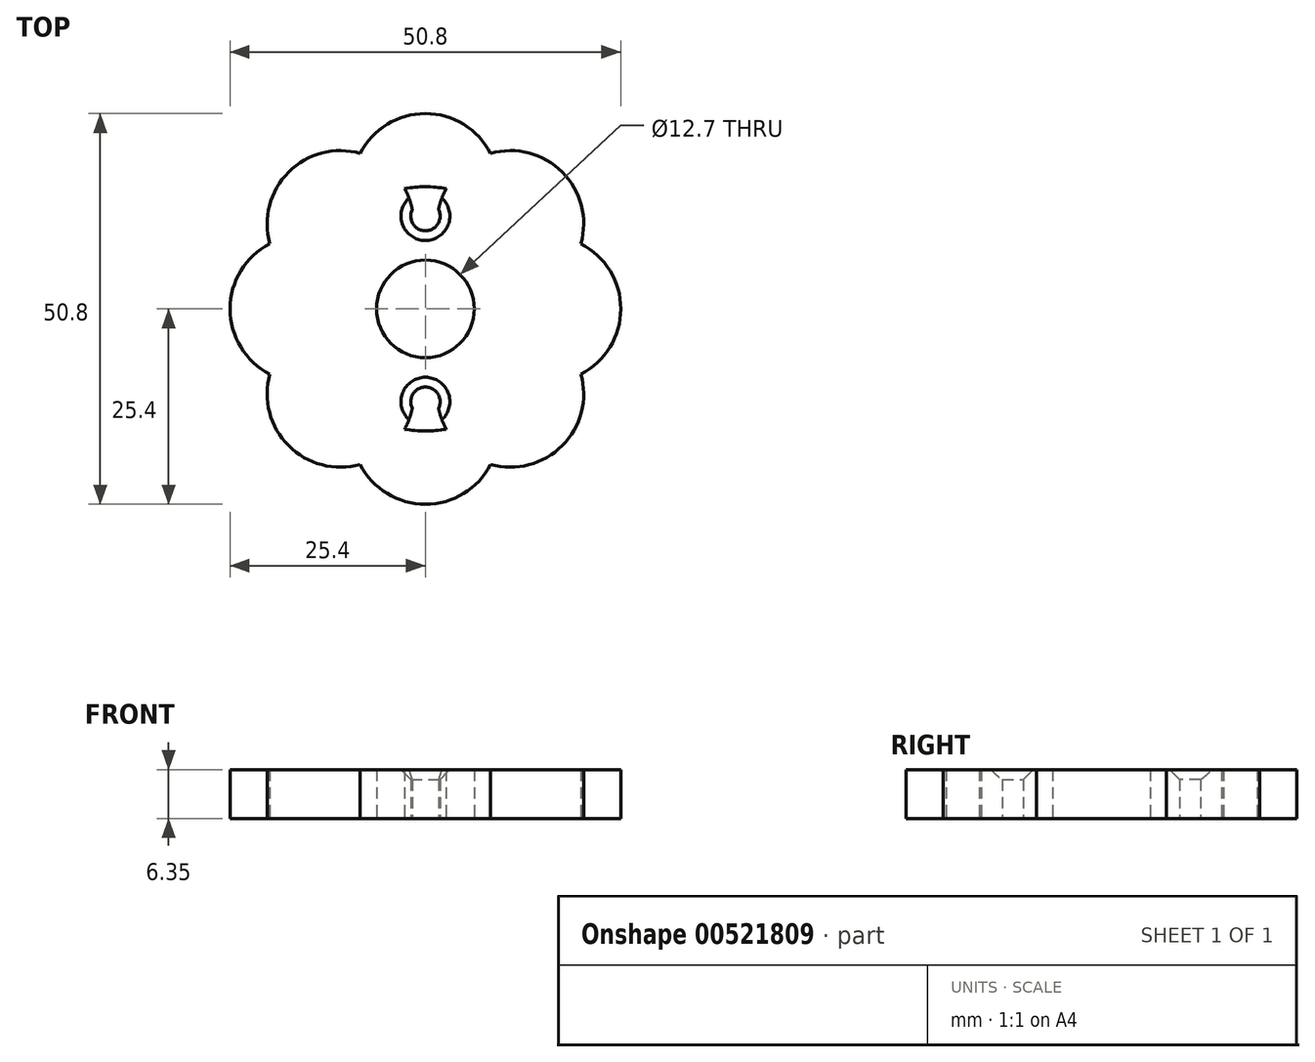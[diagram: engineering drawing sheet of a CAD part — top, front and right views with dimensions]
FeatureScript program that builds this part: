
annotation { "Feature Type Name" : "Feature", "Feature Type Description" : "" }
export const myFeature = defineFeature(function(context is Context, id is Id, definition is map)
    precondition{}
    {
        {
            var Q0;
            Q0=qCreatedBy(makeId("Top.planeOp"),FACE);
            var sketch = newSketch(context, id + "F0", { "sketchPlane" : qUnion([Q0])});
            skCircle(sketch, "E0", {"center": v(0, 0) * mm, "radius": 15.88 * mm});
            skLineSegment(sketch, "E1", {"start": v(0, 0) * mm, "end": v(15.88, 0) * mm});
            skLineSegment(sketch, "E2", {"start": v(0, 0) * mm, "end": v(0, -15.88) * mm});
            skLineSegment(sketch, "E3", {"start": v(0, 0) * mm, "end": v(-15.88, 0) * mm});
            skLineSegment(sketch, "E4", {"start": v(0, 0) * mm, "end": v(0, 15.88) * mm});
            skCircle(sketch, "E5", {"center": v(0, 15.88) * mm, "radius": 9.53 * mm});
            skCircle(sketch, "E6", {"center": v(15.88, 0) * mm, "radius": 9.53 * mm});
            skCircle(sketch, "E7", {"center": v(0, -15.88) * mm, "radius": 9.53 * mm});
            skCircle(sketch, "E8", {"center": v(-15.88, 0) * mm, "radius": 9.53 * mm});
            skLineSegment(sketch, "E9", {"start": v(-9.09, 13.02) * mm, "end": v(-13.02, 9.09) * mm});
            skLineSegment(sketch, "E10", {"start": v(9.09, 13.02) * mm, "end": v(13.02, 9.09) * mm});
            skLineSegment(sketch, "E11", {"start": v(13.02, -9.09) * mm, "end": v(9.09, -13.02) * mm});
            skLineSegment(sketch, "E12", {"start": v(-13.02, -9.09) * mm, "end": v(-9.09, -13.02) * mm});
            skPoint(sketch, "E13.centerSnap0", {"position": v(-11.05, 11.05) * mm});
            skCircle(sketch, "E14", {"center": v(11.05, 11.05) * mm, "radius": 9.53 * mm});
            skCircle(sketch, "E15", {"center": v(11.05, -11.05) * mm, "radius": 9.53 * mm});
            skCircle(sketch, "E16", {"center": v(-11.05, -11.05) * mm, "radius": 9.53 * mm});
            skCircle(sketch, "E17", {"center": v(0, 0) * mm, "radius": 6.35 * mm});
            skCircle(sketch, "E18", {"center": v(-11.05, 11.05) * mm, "radius": 9.53 * mm});
            skLineSegment(sketch, "E19", {"start": v(0, 0) * mm, "end": v(0, 17.78) * mm});
            skLineSegment(sketch, "E20", {"start": v(0, 17.78) * mm, "end": v(0, 6.35) * mm});
            skLineSegment(sketch, "E21", {"start": v(0, 0) * mm, "end": v(0, -17.78) * mm});
            skLineSegment(sketch, "E22", {"start": v(0, -17.78) * mm, "end": v(0, -6.35) * mm});
            skCircle(sketch, "E23", {"center": v(0, -12.06) * mm, "radius": 1.9 * mm});
            skCircle(sketch, "E24", {"center": v(0, 12.06) * mm, "radius": 1.9 * mm});
            skSolve(sketch);
        }
        {
            var Q0;
            {var subQ3=sQuery(id+"F0.wireOp",EDGE,"E0");var subQ5=makeQuery(id+"F0.imprint","INTERSECT",VERTEX,{"derivedFrom":[subQ3,sQuery(id+"F0.wireOp",EDGE,"E20")]});Q0=makeQuery(id+"F0.imprint","IMPRINT",FACE,{"disambiguationData":[TD([[makeQuery(id+"F0.imprint","IMPRINT",EDGE,{"disambiguationData":[TD([[subQ5,1.0]])],"derivedFrom":subQ3}),-1.0]])]});}
            var Q1;
            {var subQ0=sQuery(id+"F0.wireOp",EDGE,"E5");var subQ3=sQuery(id+"F0.wireOp",EDGE,"E14");var subQ5=makeQuery(id+"F0.imprint","INTERSECT",VERTEX,{"disambiguationData":[OD(0.0)],"derivedFrom":[subQ0,subQ3]});Q1=makeQuery(id+"F0.imprint","IMPRINT",FACE,{"disambiguationData":[TD([[makeQuery(id+"F0.imprint","IMPRINT",EDGE,{"disambiguationData":[TD([[subQ5,-1.0]])],"derivedFrom":subQ3}),1.0]])]});}
            var Q2;
            {var subQ1=sQuery(id+"F0.wireOp",EDGE,"E5");var subQ6=sQuery(id+"F0.wireOp",EDGE,"E14");var subQ7=makeQuery(id+"F0.imprint","INTERSECT",VERTEX,{"disambiguationData":[OD(0.0)],"derivedFrom":[subQ1,subQ6]});Q2=makeQuery(id+"F0.imprint","IMPRINT",FACE,{"disambiguationData":[TD([[makeQuery(id+"F0.imprint","IMPRINT",EDGE,{"disambiguationData":[TD([[subQ7,1.0]])],"derivedFrom":subQ6}),1.0]])]});}
            var Q3;
            {var subQ5=sQuery(id+"F0.wireOp",EDGE,"E0");var subQ7=makeQuery(id+"F0.imprint","INTERSECT",VERTEX,{"derivedFrom":[subQ5,sQuery(id+"F0.wireOp",EDGE,"E1")]});Q3=makeQuery(id+"F0.imprint","IMPRINT",FACE,{"disambiguationData":[TD([[makeQuery(id+"F0.imprint","IMPRINT",EDGE,{"disambiguationData":[TD([[subQ7,-1.0]])],"derivedFrom":subQ5}),-1.0]])]});}
            var Q4;
            {var subQ0=sQuery(id+"F0.wireOp",EDGE,"E6");var subQ3=sQuery(id+"F0.wireOp",EDGE,"E14");var subQ5=makeQuery(id+"F0.imprint","INTERSECT",VERTEX,{"disambiguationData":[OD(0.0)],"derivedFrom":[subQ0,subQ3]});Q4=makeQuery(id+"F0.imprint","IMPRINT",FACE,{"disambiguationData":[TD([[makeQuery(id+"F0.imprint","IMPRINT",EDGE,{"disambiguationData":[TD([[subQ5,1.0]])],"derivedFrom":subQ3}),1.0]])]});}
            var Q5;
            {var subQ0=sQuery(id+"F0.wireOp",EDGE,"E6");var subQ3=sQuery(id+"F0.wireOp",EDGE,"E15");var subQ5=makeQuery(id+"F0.imprint","INTERSECT",VERTEX,{"disambiguationData":[OD(0.0)],"derivedFrom":[subQ0,subQ3]});Q5=makeQuery(id+"F0.imprint","IMPRINT",FACE,{"disambiguationData":[TD([[makeQuery(id+"F0.imprint","IMPRINT",EDGE,{"disambiguationData":[TD([[subQ5,-1.0]])],"derivedFrom":subQ3}),1.0]])]});}
            var Q6;
            {var subQ1=sQuery(id+"F0.wireOp",EDGE,"E6");var subQ6=sQuery(id+"F0.wireOp",EDGE,"E15");var subQ7=makeQuery(id+"F0.imprint","INTERSECT",VERTEX,{"disambiguationData":[OD(0.0)],"derivedFrom":[subQ1,subQ6]});Q6=makeQuery(id+"F0.imprint","IMPRINT",FACE,{"disambiguationData":[TD([[makeQuery(id+"F0.imprint","IMPRINT",EDGE,{"disambiguationData":[TD([[subQ7,1.0]])],"derivedFrom":subQ6}),1.0]])]});}
            var Q7;
            {var subQ5=sQuery(id+"F0.wireOp",EDGE,"E0");var subQ6=makeQuery(id+"F0.imprint","INTERSECT",VERTEX,{"derivedFrom":[subQ5,sQuery(id+"F0.wireOp",EDGE,"E22")]});Q7=makeQuery(id+"F0.imprint","IMPRINT",FACE,{"disambiguationData":[TD([[makeQuery(id+"F0.imprint","IMPRINT",EDGE,{"disambiguationData":[TD([[subQ6,1.0]])],"derivedFrom":subQ5}),-1.0]])]});}
            var Q8;
            {var subQ0=sQuery(id+"F0.wireOp",EDGE,"E7");var subQ3=sQuery(id+"F0.wireOp",EDGE,"E15");var subQ5=makeQuery(id+"F0.imprint","INTERSECT",VERTEX,{"disambiguationData":[OD(0.0)],"derivedFrom":[subQ0,subQ3]});Q8=makeQuery(id+"F0.imprint","IMPRINT",FACE,{"disambiguationData":[TD([[makeQuery(id+"F0.imprint","IMPRINT",EDGE,{"disambiguationData":[TD([[subQ5,1.0]])],"derivedFrom":subQ3}),1.0]])]});}
            var Q9;
            {var subQ4=sQuery(id+"F0.wireOp",EDGE,"E7");var subQ6=sQuery(id+"F0.wireOp",EDGE,"E16");var subQ7=makeQuery(id+"F0.imprint","INTERSECT",VERTEX,{"disambiguationData":[OD(0.0)],"derivedFrom":[subQ4,subQ6]});Q9=makeQuery(id+"F0.imprint","IMPRINT",FACE,{"disambiguationData":[TD([[makeQuery(id+"F0.imprint","IMPRINT",EDGE,{"disambiguationData":[TD([[subQ7,1.0]])],"derivedFrom":subQ6}),1.0]])]});}
            var Q10;
            {var subQ0=sQuery(id+"F0.wireOp",EDGE,"E8");var subQ3=sQuery(id+"F0.wireOp",EDGE,"E16");var subQ5=makeQuery(id+"F0.imprint","INTERSECT",VERTEX,{"disambiguationData":[OD(0.0)],"derivedFrom":[subQ0,subQ3]});Q10=makeQuery(id+"F0.imprint","IMPRINT",FACE,{"disambiguationData":[TD([[makeQuery(id+"F0.imprint","IMPRINT",EDGE,{"disambiguationData":[TD([[subQ5,1.0]])],"derivedFrom":subQ3}),1.0]])]});}
            var Q11;
            {var subQ3=sQuery(id+"F0.wireOp",EDGE,"E0");var subQ7=makeQuery(id+"F0.imprint","INTERSECT",VERTEX,{"derivedFrom":[subQ3,sQuery(id+"F0.wireOp",EDGE,"E3")]});Q11=makeQuery(id+"F0.imprint","IMPRINT",FACE,{"disambiguationData":[TD([[makeQuery(id+"F0.imprint","IMPRINT",EDGE,{"disambiguationData":[TD([[subQ7,1.0]])],"derivedFrom":subQ3}),-1.0]])]});}
            var Q12;
            {var subQ0=sQuery(id+"F0.wireOp",EDGE,"E8");var subQ3=sQuery(id+"F0.wireOp",EDGE,"E18");var subQ5=makeQuery(id+"F0.imprint","INTERSECT",VERTEX,{"disambiguationData":[OD(0.0)],"derivedFrom":[subQ0,subQ3]});Q12=makeQuery(id+"F0.imprint","IMPRINT",FACE,{"disambiguationData":[TD([[makeQuery(id+"F0.imprint","IMPRINT",EDGE,{"disambiguationData":[TD([[subQ5,-1.0]])],"derivedFrom":subQ3}),1.0]])]});}
            var Q13;
            {var subQ1=sQuery(id+"F0.wireOp",EDGE,"E5");var subQ6=sQuery(id+"F0.wireOp",EDGE,"E18");var subQ8=makeQuery(id+"F0.imprint","INTERSECT",VERTEX,{"disambiguationData":[OD(0.0)],"derivedFrom":[subQ1,subQ6]});Q13=makeQuery(id+"F0.imprint","IMPRINT",FACE,{"disambiguationData":[TD([[makeQuery(id+"F0.imprint","IMPRINT",EDGE,{"disambiguationData":[TD([[subQ8,-1.0]])],"derivedFrom":subQ6}),1.0]])]});}
            var Q14;
            {var subQ4=sQuery(id+"F0.wireOp",EDGE,"E9");Q14=makeQuery(id+"F0.imprint","IMPRINT",FACE,{"disambiguationData":[TD([[makeQuery(id+"F0.imprint","IMPRINT",EDGE,{"derivedFrom":subQ4}),1.0]])]});}
            var Q15;
            {var subQ0=sQuery(id+"F0.wireOp",EDGE,"E18");var subQ1=sQuery(id+"F0.wireOp",EDGE,"E0");var subQ2=makeQuery(id+"F0.imprint","INTERSECT",VERTEX,{"disambiguationData":[OD(0.0)],"derivedFrom":[subQ1,subQ0]});Q15=makeQuery(id+"F0.imprint","IMPRINT",FACE,{"disambiguationData":[TD([[makeQuery(id+"F0.imprint","IMPRINT",EDGE,{"disambiguationData":[TD([[subQ2,1.0]])],"derivedFrom":subQ0}),1.0]])]});}
            var Q16;
            {var subQ0=sQuery(id+"F0.wireOp",EDGE,"E5");var subQ3=sQuery(id+"F0.wireOp",EDGE,"E18");var subQ5=makeQuery(id+"F0.imprint","INTERSECT",VERTEX,{"disambiguationData":[OD(0.0)],"derivedFrom":[subQ0,subQ3]});Q16=makeQuery(id+"F0.imprint","IMPRINT",FACE,{"disambiguationData":[TD([[makeQuery(id+"F0.imprint","IMPRINT",EDGE,{"disambiguationData":[TD([[subQ5,1.0]])],"derivedFrom":subQ3}),1.0]])]});}
            var Q17;
            {var subQ1=sQuery(id+"F0.wireOp",EDGE,"E5");var subQ3=sQuery(id+"F0.wireOp",EDGE,"E14");var subQ4=makeQuery(id+"F0.imprint","INTERSECT",VERTEX,{"disambiguationData":[OD(1.0)],"derivedFrom":[subQ1,subQ3]});Q17=makeQuery(id+"F0.imprint","IMPRINT",FACE,{"disambiguationData":[TD([[makeQuery(id+"F0.imprint","IMPRINT",EDGE,{"disambiguationData":[TD([[subQ4,1.0]])],"derivedFrom":subQ3}),-1.0]])]});}
            var Q18;
            {var subQ1=sQuery(id+"F0.wireOp",EDGE,"E5");var subQ3=sQuery(id+"F0.wireOp",EDGE,"E18");var subQ4=makeQuery(id+"F0.imprint","INTERSECT",VERTEX,{"disambiguationData":[OD(1.0)],"derivedFrom":[subQ1,subQ3]});Q18=makeQuery(id+"F0.imprint","IMPRINT",FACE,{"disambiguationData":[TD([[makeQuery(id+"F0.imprint","IMPRINT",EDGE,{"disambiguationData":[TD([[subQ4,-1.0]])],"derivedFrom":subQ3}),-1.0]])]});}
            var Q19;
            {var subQ0=sQuery(id+"F0.wireOp",EDGE,"E20");var subQ1=sQuery(id+"F0.wireOp",EDGE,"E0");var subQ2=makeQuery(id+"F0.imprint","INTERSECT",VERTEX,{"derivedFrom":[subQ1,subQ0]});Q19=makeQuery(id+"F0.imprint","IMPRINT",FACE,{"disambiguationData":[TD([[makeQuery(id+"F0.imprint","IMPRINT",EDGE,{"disambiguationData":[TD([[subQ2,-1.0]])],"derivedFrom":subQ1}),1.0]])]});}
            var Q20;
            {var subQ0=sQuery(id+"F0.wireOp",EDGE,"E20");var subQ1=sQuery(id+"F0.wireOp",EDGE,"E0");var subQ2=makeQuery(id+"F0.imprint","INTERSECT",VERTEX,{"derivedFrom":[subQ1,subQ0]});Q20=makeQuery(id+"F0.imprint","IMPRINT",FACE,{"disambiguationData":[TD([[makeQuery(id+"F0.imprint","IMPRINT",EDGE,{"disambiguationData":[TD([[subQ2,1.0]])],"derivedFrom":subQ1}),1.0]])]});}
            var Q21;
            {var subQ0=sQuery(id+"F0.wireOp",EDGE,"E14");var subQ1=sQuery(id+"F0.wireOp",EDGE,"E0");var subQ2=makeQuery(id+"F0.imprint","INTERSECT",VERTEX,{"disambiguationData":[OD(1.0)],"derivedFrom":[subQ1,subQ0]});Q21=makeQuery(id+"F0.imprint","IMPRINT",FACE,{"disambiguationData":[TD([[makeQuery(id+"F0.imprint","IMPRINT",EDGE,{"disambiguationData":[TD([[subQ2,-1.0]])],"derivedFrom":subQ0}),1.0]])]});}
            var Q22;
            {var subQ5=sQuery(id+"F0.wireOp",EDGE,"E10");Q22=makeQuery(id+"F0.imprint","IMPRINT",FACE,{"disambiguationData":[TD([[makeQuery(id+"F0.imprint","IMPRINT",EDGE,{"derivedFrom":subQ5}),-1.0]])]});}
            var Q23;
            {var subQ1=sQuery(id+"F0.wireOp",EDGE,"E0");var subQ3=sQuery(id+"F0.wireOp",EDGE,"E14");var subQ4=makeQuery(id+"F0.imprint","INTERSECT",VERTEX,{"disambiguationData":[OD(0.0)],"derivedFrom":[subQ1,subQ3]});Q23=makeQuery(id+"F0.imprint","IMPRINT",FACE,{"disambiguationData":[TD([[makeQuery(id+"F0.imprint","IMPRINT",EDGE,{"disambiguationData":[TD([[subQ4,1.0]])],"derivedFrom":subQ3}),1.0]])]});}
            var Q24;
            {var subQ0=sQuery(id+"F0.wireOp",EDGE,"E1");var subQ1=sQuery(id+"F0.wireOp",EDGE,"E0");var subQ2=makeQuery(id+"F0.imprint","INTERSECT",VERTEX,{"derivedFrom":[subQ1,subQ0]});Q24=makeQuery(id+"F0.imprint","IMPRINT",FACE,{"disambiguationData":[TD([[makeQuery(id+"F0.imprint","IMPRINT",EDGE,{"disambiguationData":[TD([[subQ2,-1.0]])],"derivedFrom":subQ1}),1.0]])]});}
            var Q25;
            {var subQ1=sQuery(id+"F0.wireOp",EDGE,"E0");var subQ3=sQuery(id+"F0.wireOp",EDGE,"E15");var subQ4=makeQuery(id+"F0.imprint","INTERSECT",VERTEX,{"disambiguationData":[OD(1.0)],"derivedFrom":[subQ1,subQ3]});Q25=makeQuery(id+"F0.imprint","IMPRINT",FACE,{"disambiguationData":[TD([[makeQuery(id+"F0.imprint","IMPRINT",EDGE,{"disambiguationData":[TD([[subQ4,-1.0]])],"derivedFrom":subQ3}),1.0]])]});}
            var Q26;
            {var subQ0=sQuery(id+"F0.wireOp",EDGE,"E1");var subQ1=sQuery(id+"F0.wireOp",EDGE,"E0");var subQ2=makeQuery(id+"F0.imprint","INTERSECT",VERTEX,{"derivedFrom":[subQ1,subQ0]});Q26=makeQuery(id+"F0.imprint","IMPRINT",FACE,{"disambiguationData":[TD([[makeQuery(id+"F0.imprint","IMPRINT",EDGE,{"disambiguationData":[TD([[subQ2,1.0]])],"derivedFrom":subQ1}),1.0]])]});}
            var Q27;
            {var subQ0=sQuery(id+"F0.wireOp",EDGE,"E11");Q27=makeQuery(id+"F0.imprint","IMPRINT",FACE,{"disambiguationData":[TD([[makeQuery(id+"F0.imprint","IMPRINT",EDGE,{"derivedFrom":subQ0}),-1.0]])]});}
            var Q28;
            {var subQ0=sQuery(id+"F0.wireOp",EDGE,"E15");var subQ5=sQuery(id+"F0.wireOp",EDGE,"E7");var subQ7=makeQuery(id+"F0.imprint","INTERSECT",VERTEX,{"disambiguationData":[OD(1.0)],"derivedFrom":[subQ5,subQ0]});Q28=makeQuery(id+"F0.imprint","IMPRINT",FACE,{"disambiguationData":[TD([[makeQuery(id+"F0.imprint","IMPRINT",EDGE,{"disambiguationData":[TD([[subQ7,-1.0]])],"derivedFrom":subQ0}),1.0]])]});}
            var Q29;
            {var subQ1=sQuery(id+"F0.wireOp",EDGE,"E7");var subQ3=sQuery(id+"F0.wireOp",EDGE,"E15");var subQ4=makeQuery(id+"F0.imprint","INTERSECT",VERTEX,{"disambiguationData":[OD(1.0)],"derivedFrom":[subQ1,subQ3]});Q29=makeQuery(id+"F0.imprint","IMPRINT",FACE,{"disambiguationData":[TD([[makeQuery(id+"F0.imprint","IMPRINT",EDGE,{"disambiguationData":[TD([[subQ4,-1.0]])],"derivedFrom":subQ3}),-1.0]])]});}
            var Q30;
            {var subQ1=sQuery(id+"F0.wireOp",EDGE,"E7");var subQ3=sQuery(id+"F0.wireOp",EDGE,"E16");var subQ4=makeQuery(id+"F0.imprint","INTERSECT",VERTEX,{"disambiguationData":[OD(1.0)],"derivedFrom":[subQ1,subQ3]});Q30=makeQuery(id+"F0.imprint","IMPRINT",FACE,{"disambiguationData":[TD([[makeQuery(id+"F0.imprint","IMPRINT",EDGE,{"disambiguationData":[TD([[subQ4,1.0]])],"derivedFrom":subQ3}),-1.0]])]});}
            var Q31;
            {var subQ0=sQuery(id+"F0.wireOp",EDGE,"E16");var subQ5=sQuery(id+"F0.wireOp",EDGE,"E7");var subQ6=makeQuery(id+"F0.imprint","INTERSECT",VERTEX,{"disambiguationData":[OD(1.0)],"derivedFrom":[subQ5,subQ0]});Q31=makeQuery(id+"F0.imprint","IMPRINT",FACE,{"disambiguationData":[TD([[makeQuery(id+"F0.imprint","IMPRINT",EDGE,{"disambiguationData":[TD([[subQ6,1.0]])],"derivedFrom":subQ0}),1.0]])]});}
            var Q32;
            {var subQ5=sQuery(id+"F0.wireOp",EDGE,"E12");Q32=makeQuery(id+"F0.imprint","IMPRINT",FACE,{"disambiguationData":[TD([[makeQuery(id+"F0.imprint","IMPRINT",EDGE,{"derivedFrom":subQ5}),1.0]])]});}
            var Q33;
            {var subQ1=sQuery(id+"F0.wireOp",EDGE,"E0");var subQ3=sQuery(id+"F0.wireOp",EDGE,"E16");var subQ4=makeQuery(id+"F0.imprint","INTERSECT",VERTEX,{"disambiguationData":[OD(0.0)],"derivedFrom":[subQ1,subQ3]});Q33=makeQuery(id+"F0.imprint","IMPRINT",FACE,{"disambiguationData":[TD([[makeQuery(id+"F0.imprint","IMPRINT",EDGE,{"disambiguationData":[TD([[subQ4,1.0]])],"derivedFrom":subQ3}),1.0]])]});}
            var Q34;
            {var subQ0=sQuery(id+"F0.wireOp",EDGE,"E3");var subQ1=sQuery(id+"F0.wireOp",EDGE,"E0");var subQ2=makeQuery(id+"F0.imprint","INTERSECT",VERTEX,{"derivedFrom":[subQ1,subQ0]});Q34=makeQuery(id+"F0.imprint","IMPRINT",FACE,{"disambiguationData":[TD([[makeQuery(id+"F0.imprint","IMPRINT",EDGE,{"disambiguationData":[TD([[subQ2,-1.0]])],"derivedFrom":subQ1}),1.0]])]});}
            var Q35;
            {var subQ0=sQuery(id+"F0.wireOp",EDGE,"E3");var subQ1=sQuery(id+"F0.wireOp",EDGE,"E0");var subQ2=makeQuery(id+"F0.imprint","INTERSECT",VERTEX,{"derivedFrom":[subQ1,subQ0]});Q35=makeQuery(id+"F0.imprint","IMPRINT",FACE,{"disambiguationData":[TD([[makeQuery(id+"F0.imprint","IMPRINT",EDGE,{"disambiguationData":[TD([[subQ2,1.0]])],"derivedFrom":subQ1}),1.0]])]});}
            var Q36;
            {var subQ1=sQuery(id+"F0.wireOp",EDGE,"E0");var subQ3=sQuery(id+"F0.wireOp",EDGE,"E18");var subQ4=makeQuery(id+"F0.imprint","INTERSECT",VERTEX,{"disambiguationData":[OD(1.0)],"derivedFrom":[subQ1,subQ3]});Q36=makeQuery(id+"F0.imprint","IMPRINT",FACE,{"disambiguationData":[TD([[makeQuery(id+"F0.imprint","IMPRINT",EDGE,{"disambiguationData":[TD([[subQ4,-1.0]])],"derivedFrom":subQ3}),1.0]])]});}
            var Q37;
            {var subQ0=sQuery(id+"F0.wireOp",EDGE,"E18");var subQ1=sQuery(id+"F0.wireOp",EDGE,"E8");var subQ2=makeQuery(id+"F0.imprint","INTERSECT",VERTEX,{"disambiguationData":[OD(1.0)],"derivedFrom":[subQ1,subQ0]});Q37=makeQuery(id+"F0.imprint","IMPRINT",FACE,{"disambiguationData":[TD([[makeQuery(id+"F0.imprint","IMPRINT",EDGE,{"disambiguationData":[TD([[subQ2,-1.0]])],"derivedFrom":subQ0}),-1.0]])]});}
            var Q38;
            {var subQ1=sQuery(id+"F0.wireOp",EDGE,"E5");var subQ3=sQuery(id+"F0.wireOp",EDGE,"E18");var subQ4=makeQuery(id+"F0.imprint","INTERSECT",VERTEX,{"disambiguationData":[OD(1.0)],"derivedFrom":[subQ1,subQ3]});Q38=makeQuery(id+"F0.imprint","IMPRINT",FACE,{"disambiguationData":[TD([[makeQuery(id+"F0.imprint","IMPRINT",EDGE,{"disambiguationData":[TD([[subQ4,1.0]])],"derivedFrom":subQ3}),-1.0]])]});}
            var Q39;
            {var subQ1=sQuery(id+"F0.wireOp",EDGE,"E5");var subQ3=sQuery(id+"F0.wireOp",EDGE,"E14");var subQ4=makeQuery(id+"F0.imprint","INTERSECT",VERTEX,{"disambiguationData":[OD(1.0)],"derivedFrom":[subQ1,subQ3]});Q39=makeQuery(id+"F0.imprint","IMPRINT",FACE,{"disambiguationData":[TD([[makeQuery(id+"F0.imprint","IMPRINT",EDGE,{"disambiguationData":[TD([[subQ4,-1.0]])],"derivedFrom":subQ3}),-1.0]])]});}
            var Q40;
            {var subQ0=sQuery(id+"F0.wireOp",EDGE,"E14");var subQ1=sQuery(id+"F0.wireOp",EDGE,"E6");var subQ2=makeQuery(id+"F0.imprint","INTERSECT",VERTEX,{"disambiguationData":[OD(1.0)],"derivedFrom":[subQ1,subQ0]});Q40=makeQuery(id+"F0.imprint","IMPRINT",FACE,{"disambiguationData":[TD([[makeQuery(id+"F0.imprint","IMPRINT",EDGE,{"disambiguationData":[TD([[subQ2,1.0]])],"derivedFrom":subQ0}),-1.0]])]});}
            var Q41;
            {var subQ0=sQuery(id+"F0.wireOp",EDGE,"E15");var subQ1=sQuery(id+"F0.wireOp",EDGE,"E6");var subQ2=makeQuery(id+"F0.imprint","INTERSECT",VERTEX,{"disambiguationData":[OD(1.0)],"derivedFrom":[subQ1,subQ0]});Q41=makeQuery(id+"F0.imprint","IMPRINT",FACE,{"disambiguationData":[TD([[makeQuery(id+"F0.imprint","IMPRINT",EDGE,{"disambiguationData":[TD([[subQ2,-1.0]])],"derivedFrom":subQ0}),-1.0]])]});}
            var Q42;
            {var subQ1=sQuery(id+"F0.wireOp",EDGE,"E7");var subQ3=sQuery(id+"F0.wireOp",EDGE,"E15");var subQ4=makeQuery(id+"F0.imprint","INTERSECT",VERTEX,{"disambiguationData":[OD(1.0)],"derivedFrom":[subQ1,subQ3]});Q42=makeQuery(id+"F0.imprint","IMPRINT",FACE,{"disambiguationData":[TD([[makeQuery(id+"F0.imprint","IMPRINT",EDGE,{"disambiguationData":[TD([[subQ4,1.0]])],"derivedFrom":subQ3}),-1.0]])]});}
            var Q43;
            {var subQ1=sQuery(id+"F0.wireOp",EDGE,"E7");var subQ3=sQuery(id+"F0.wireOp",EDGE,"E16");var subQ4=makeQuery(id+"F0.imprint","INTERSECT",VERTEX,{"disambiguationData":[OD(1.0)],"derivedFrom":[subQ1,subQ3]});Q43=makeQuery(id+"F0.imprint","IMPRINT",FACE,{"disambiguationData":[TD([[makeQuery(id+"F0.imprint","IMPRINT",EDGE,{"disambiguationData":[TD([[subQ4,-1.0]])],"derivedFrom":subQ3}),-1.0]])]});}
            var Q44;
            {var subQ0=sQuery(id+"F0.wireOp",EDGE,"E16");var subQ1=sQuery(id+"F0.wireOp",EDGE,"E8");var subQ2=makeQuery(id+"F0.imprint","INTERSECT",VERTEX,{"disambiguationData":[OD(1.0)],"derivedFrom":[subQ1,subQ0]});Q44=makeQuery(id+"F0.imprint","IMPRINT",FACE,{"disambiguationData":[TD([[makeQuery(id+"F0.imprint","IMPRINT",EDGE,{"disambiguationData":[TD([[subQ2,1.0]])],"derivedFrom":subQ0}),-1.0]])]});}
            var Q45;
            {var subQ0=sQuery(id+"F0.wireOp",EDGE,"E7");var subQ3=sQuery(id+"F0.wireOp",EDGE,"E16");var subQ5=makeQuery(id+"F0.imprint","INTERSECT",VERTEX,{"disambiguationData":[OD(0.0)],"derivedFrom":[subQ0,subQ3]});Q45=makeQuery(id+"F0.imprint","IMPRINT",FACE,{"disambiguationData":[TD([[makeQuery(id+"F0.imprint","IMPRINT",EDGE,{"disambiguationData":[TD([[subQ5,-1.0]])],"derivedFrom":subQ3}),1.0]])]});}
            var Q46;
            {var subQ0=sQuery(id+"F0.wireOp",EDGE,"E22");var subQ1=sQuery(id+"F0.wireOp",EDGE,"E0");var subQ2=makeQuery(id+"F0.imprint","INTERSECT",VERTEX,{"derivedFrom":[subQ1,subQ0]});Q46=makeQuery(id+"F0.imprint","IMPRINT",FACE,{"disambiguationData":[TD([[makeQuery(id+"F0.imprint","IMPRINT",EDGE,{"disambiguationData":[TD([[subQ2,1.0]])],"derivedFrom":subQ1}),1.0]])]});}
            var Q47;
            {var subQ0=sQuery(id+"F0.wireOp",EDGE,"E22");var subQ1=sQuery(id+"F0.wireOp",EDGE,"E0");var subQ2=makeQuery(id+"F0.imprint","INTERSECT",VERTEX,{"derivedFrom":[subQ1,subQ0]});Q47=makeQuery(id+"F0.imprint","IMPRINT",FACE,{"disambiguationData":[TD([[makeQuery(id+"F0.imprint","IMPRINT",EDGE,{"disambiguationData":[TD([[subQ2,-1.0]])],"derivedFrom":subQ1}),1.0]])]});}
            var Q48;
            {var subQ0=sQuery(id+"F0.wireOp",EDGE,"E11");Q48=makeQuery(id+"F0.imprint","IMPRINT",FACE,{"disambiguationData":[TD([[makeQuery(id+"F0.imprint","IMPRINT",EDGE,{"derivedFrom":subQ0}),1.0]])]});}
            var Q49;
            {var subQ0=sQuery(id+"F0.wireOp",EDGE,"E10");Q49=makeQuery(id+"F0.imprint","IMPRINT",FACE,{"disambiguationData":[TD([[makeQuery(id+"F0.imprint","IMPRINT",EDGE,{"derivedFrom":subQ0}),1.0]])]});}
            var Q50;
            {var subQ0=sQuery(id+"F0.wireOp",EDGE,"E9");Q50=makeQuery(id+"F0.imprint","IMPRINT",FACE,{"disambiguationData":[TD([[makeQuery(id+"F0.imprint","IMPRINT",EDGE,{"derivedFrom":subQ0}),-1.0]])]});}
            var Q51;
            {var subQ0=sQuery(id+"F0.wireOp",EDGE,"E12");Q51=makeQuery(id+"F0.imprint","IMPRINT",FACE,{"disambiguationData":[TD([[makeQuery(id+"F0.imprint","IMPRINT",EDGE,{"derivedFrom":subQ0}),-1.0]])]});}
            extrude(context, id + "F1", {"entities" : qUnion([Q0, Q1, Q2, Q3, Q4, Q5, Q6, Q7, Q8, Q9, Q10, Q11, Q12, Q13, Q14, Q15, Q16, Q17, Q18, Q19, Q20, Q21, Q22, Q23, Q24, Q25, Q26, Q27, Q28, Q29, Q30, Q31, Q32, Q33, Q34, Q35, Q36, Q37, Q38, Q39, Q40, Q41, Q42, Q43, Q44, Q45, Q46, Q47, Q48, Q49, Q50, Q51]), "depth" : 6.35 * mm, "offsetDistance" : 25.4 * mm});
        }
        {
            var Q0;
            Q0=makeQuery(id+"F1.opExtrude","CAP_EDGE",EDGE,{"disambiguationData":[OSD([sQuery(id+"F0.wireOp",EDGE,"E23")])],"isStart":false});
            var Q1;
            Q1=makeQuery(id+"F1.opExtrude","CAP_EDGE",EDGE,{"disambiguationData":[OSD([sQuery(id+"F0.wireOp",EDGE,"E24")])],"isStart":false});
            chamfer(context, id + "F2", {"entities" : qUnion([Q0, Q1]), "width" : 1.27 * mm, "tangentPropagation" : true});
        }
    });
